# Revit family: WL2102
name_source: partatom
category: Communication Devices
revit_build: Autodesk Revit Architecture 2012 (Build: 20110309_2315(x64)
units: mm (PartAtom-declared; Revit-internal decimal feet)

## types (1)
- WL2102
    Coverage Horizontal = 140.00°
    Coverage Vertical = 10.00°
    Default Elevation = 0"
    Depth = 20.25"
    Description = Dual 10" Line Array Loudspeaker Element
    Enclosure Depth = 18.125"
    Enclosure Front Height = 10.75"
    Enclosure Front Width = 27.5"
    Enclosure Material = Black Finish
    Enclosure Mid Depth = 1"
    Enclosure Rear Height = 7.641"
    Enclosure Rear Width = 26.75"
    Grille Depth = 1.125"
    Grille Extent Height = 8.373"
    Grille Material = Black Grille
    Grille Width = 26"
    Height = 10.75"
    Impedance = 16
    Impedance 2 = 16
    Impedance 3 = 16
    Manufacturer = QSC Audio Products, LLC
    Manufacturer URL = www.qscaudio.com
    Model = WL2102
    Power Handling = 400
    Power Handling 2 = 400
    Power Handling 3 = 80
    Product Documentation Link = http://media.qscaudio.com
    Product Page URL = http://www.qscaudio.com
    Regulatory Compliance = RoHS
    SPL Max = 133
    Sensitivity = 98
    Sensitivity 2 = 98
    Sensitivity 3 = 107.5
    URL = http://www.qscaudio.com
    Weight Dimensional (kg) = 41.4
    Weight Dimensional (lb) = 91
    Weight Product (kg) = 37.7
    Weight Product (lb) = 83
    Width = 27.5"

## geometry (parser evidence)
native form markers: Blend x2, Sweep x1
no freeform markers — native parametric forms only
